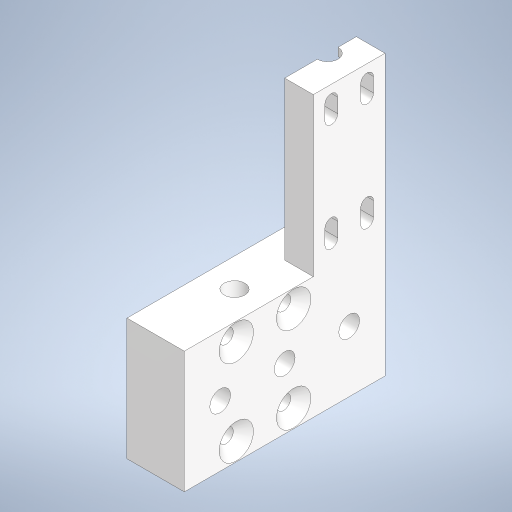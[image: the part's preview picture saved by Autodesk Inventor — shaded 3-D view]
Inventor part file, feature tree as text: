
AUTODESK INVENTOR PART (.ipt)
format: ipt  version: 2024.1 (Build 281209000, 209)  size: 376,320 bytes
history: native  units: in
note: dims shown in document units (in); Inventor stores cm internally (conversion verified against a paired STEP export)
features: extrude x7, sketch x7, chamfer x2
ambient origin geometry x8: Origin, YZ Plane, XZ Plane, XY Plane, X Axis, Y Axis, Z Axis, Center Point
bodies: Solid1 (feature_tree)
feature tree (16):
  extrude  "Extrusion1"  Depth=1.1024in
  extrude  "Extrusion2"  Depth=0.3937in
  extrude  "Extrusion3"  Depth=0.315in TaperAngle=0.0deg
  extrude  "Extrusion4"  TaperAngle=0.0deg  [1 undecoded]
  extrude  "Extrusion5"  Depth=0.0787in
  chamfer  "Chamfer1"  Distance=0.0984in
  extrude  "Extrusion7"  Depth=0.0354in
  chamfer  "Chamfer3"  Distance=0.0984in
  extrude  "Extrusion8"  Depth=0.0354in
  sketch  "Sketch1"  dims[d0=0.6693in d1=1.1024in]
  sketch  "Sketch2"  dims[d2=0.315in d3=0.0in d4=0.3937in]
  sketch  "Sketch3"  dims[d5=0.8661in d6=0.315in d7=0.0in]
  sketch  "Sketch4"  dims[d8=0.1575in d9=0.0in d10=0.0in]
  sketch  "Sketch5"  dims[d11=0.0787in d13=0.0787in]
  sketch  "Sketch8"  dims[d14=0.0787in]
  sketch  "Sketch9"  dims[d15=0.0787in d16=0.0984in d17=0.0984in d18=0.0984in d19=0.0984in d20=0.2854in d21=0.2854in d22=0.315in d23=0.315in d24=0.0in d25=0.0in d26=0.1142in d27=0.1142in d28=0.1575in d29=0.1575in d30=0.6693in d31=0.0in d32=0.0in d33=0.0079in d34=0.0787in d35=45.0deg d53=0.3346in d54=0.3346in d55=0.3346in d56=0.1142in d57=0.1142in d58=0.1142in d59=0.1969in d60=0.5512in d61=0.1969in d62=0.0in d63=0.0in d64=0.0551in d65=0.0787in d66=45.0deg d70=0.0709in d71=0.0709in d72=0.0709in d73=0.0709in d74=0.0984in d75=0.0787in d76=0.0787in d77=0.0984in d78=0.0984in d79=0.0984in d80=0.5906in d81=0.5906in d82=0.0709in d83=0.0709in d84=0.0709in d85=0.0787in d86=0.0787in d87=0.0787in d88=0.0354in d89=0.0354in d90=0.0in d91=0.0in]
note: 1 required parameter value undecoded (feature->parameter linkage not recoverable at this tier; creation-order binding heuristic only, values carry confidence <= 0.55)
